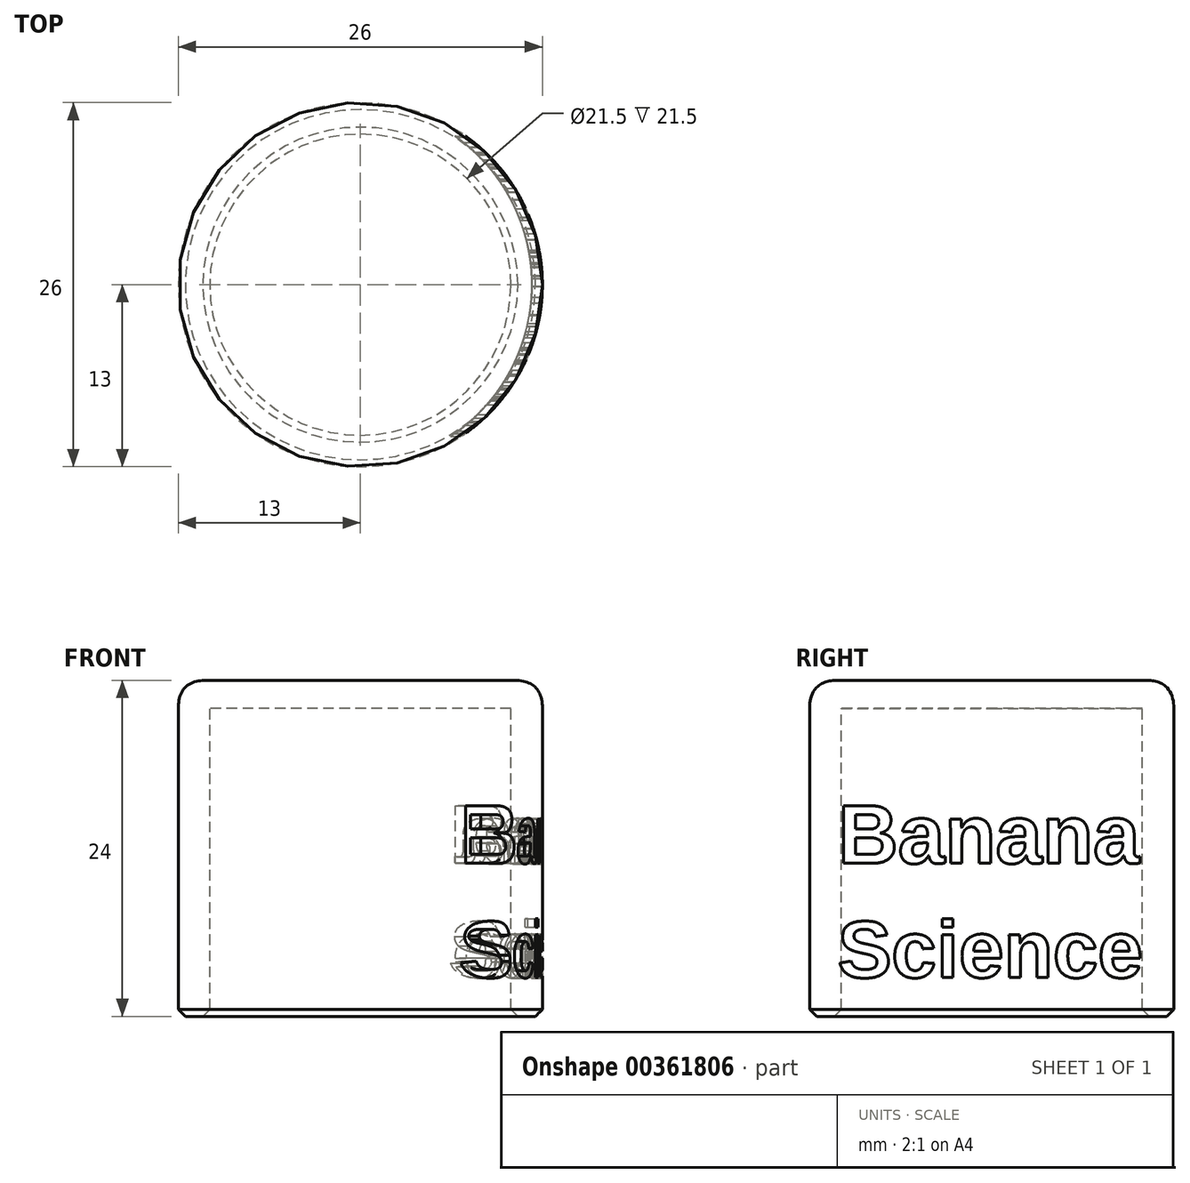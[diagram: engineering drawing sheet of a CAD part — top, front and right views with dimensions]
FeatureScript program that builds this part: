
annotation { "Feature Type Name" : "Feature", "Feature Type Description" : "" }
export const myFeature = defineFeature(function(context is Context, id is Id, definition is map)
    precondition{}
    {
        {
            var Q0;
            Q0=qCreatedBy(makeId("Top.planeOp"),FACE);
            var sketch = newSketch(context, id + "F0", { "sketchPlane" : qUnion([Q0])});
            skCircle(sketch, "E0", {"center": v(0, 0) * mm, "radius": 10.75 * mm});
            skCircle(sketch, "E1", {"center": v(0, 0) * mm, "radius": 13 * mm});
            skSolve(sketch);
        }
        {
            var Q0;
            Q0=makeQuery(id+"F0.imprint","IMPRINT",FACE,{"disambiguationData":[TD([[makeQuery(id+"F0.imprint","IMPRINT",EDGE,{"derivedFrom":sQuery(id+"F0.wireOp",EDGE,"E0")}),-1.0]])]});
            extrude(context, id + "F1", {"entities" : qUnion([Q0]), "oppositeDirection" : true, "depth" : 24 * mm, "offsetDistance" : 25 * mm});
        }
        {
            var Q0;
            Q0=makeQuery(id+"F0.imprint","IMPRINT",FACE,{"disambiguationData":[TD([[makeQuery(id+"F0.imprint","IMPRINT",EDGE,{"derivedFrom":sQuery(id+"F0.wireOp",EDGE,"E0")}),1.0]])]});
            extrude(context, id + "F2", {"entities" : qUnion([Q0]), "operationType" : NewBodyOperationType.ADD, "oppositeDirection" : true, "depth" : 2 * mm, "offsetDistance" : 25 * mm});
        }
        {
            var Q0;
            Q0=makeQuery(id+"F1.opExtrude","CAP_EDGE",EDGE,{"disambiguationData":[OSD([sQuery(id+"F0.wireOp",EDGE,"E1")])],"isStart":true});
            var Q1;
            Q1=makeQuery(id+"F2.opExtrude","CAP_EDGE",EDGE,{"disambiguationData":[OSD([sQuery(id+"F0.wireOp",EDGE,"E0")])],"isStart":false});
            fillet(context, id + "F3", {"entities" : qUnion([Q0, Q1]), "radius" : 2 * mm, "tangentPropagation" : true, "rho" : 0.5, "crossSection" : FilletCrossSection.CONIC, "allowEdgeOverflow" : false});
        }
        {
            var Q0;
            Q0=makeQuery(id+"F1.opExtrude","CAP_EDGE",EDGE,{"disambiguationData":[OSD([sQuery(id+"F0.wireOp",EDGE,"E0")])],"isStart":false});
            var Q1;
            Q1=makeQuery(id+"F1.opExtrude","CAP_EDGE",EDGE,{"disambiguationData":[OSD([sQuery(id+"F0.wireOp",EDGE,"E1")])],"isStart":false});
            var Q2;
            Q2=makeQuery(id+"F2.opExtrude","CAP_EDGE",EDGE,{"disambiguationData":[OSD([sQuery(id+"F0.wireOp",EDGE,"6ru0MfPZ-ubaX-B0dC-GUrv-7Vsd5N7kwgG7")])],"isStart":true});
            var Q3;
            Q3=makeQuery(id+"F2.opExtrude","CAP_EDGE",EDGE,{"disambiguationData":[OSD([sQuery(id+"F0.wireOp",EDGE,"6ru0MfPZ-ubaX-B0dC-GUrv-7Vsd5N7kwgG7")])],"isStart":false});
            chamfer(context, id + "F4", {"entities" : qUnion([Q0, Q1, Q2, Q3]), "width" : .5 * mm, "tangentPropagation" : true});
        }
        {
            var Q0;
            Q0=qCreatedBy(makeId("Right.planeOp"),FACE);
            cPlane(context, id + "F5", {"entities" : qUnion([Q0]), "cplaneType" : CPlaneType.OFFSET, "offset" : (26 / 2) * mm, "width" : 150 * mm, "height" : 150 * mm});
        }
        {
            var Q0;
            Q0=qCreatedBy(id+"F5.planeOp",FACE);
            var sketch = newSketch(context, id + "F6", { "sketchPlane" : qUnion([Q0])});
            skText(sketch, "E2", { "text": "Banana\n", "fontName": "Arimo-Bold.ttf"});
            skText(sketch, "E3", { "text": "Science", "fontName": "Arimo-Bold.ttf"});
            skLineSegment(sketch, "E4", {"start": v(0, -6.78) * mm, "end": v(0, -2) * mm, "construction": true});
            skLineSegment(sketch, "E5", {"start": v(0, -19.22) * mm, "end": v(0, -24) * mm, "construction": true});
            const initialGuessF6  = {"E2": [-0.011, -0.01307, 1, 0, 0.0043], "E3": [-0.011, -0.02122, 1, 0, 0.00415]};
            skSetInitialGuess(sketch, initialGuessF6);
            skSolve(sketch);
        }
        {
            var Q0;
            Q0=makeQuery(id+"F6.imprint","IMPRINT",FACE,{"disambiguationData":[TD([[makeQuery(id+"F6.imprint","IMPRINT",EDGE,{"derivedFrom":sQuery(id+"F6.wireOp",EDGE,"E2.sketch_text.stroke-0")}),-1.0]])]});
            var Q1;
            Q1=makeQuery(id+"F6.imprint","IMPRINT",FACE,{"disambiguationData":[TD([[makeQuery(id+"F6.imprint","IMPRINT",EDGE,{"derivedFrom":sQuery(id+"F6.wireOp",EDGE,"E2.sketch_text.stroke-24")}),-1.0]])]});
            var Q2;
            Q2=makeQuery(id+"F6.imprint","IMPRINT",FACE,{"disambiguationData":[TD([[makeQuery(id+"F6.imprint","IMPRINT",EDGE,{"derivedFrom":sQuery(id+"F6.wireOp",EDGE,"E2.sketch_text.stroke-62")}),-1.0]])]});
            var Q3;
            Q3=makeQuery(id+"F6.imprint","IMPRINT",FACE,{"disambiguationData":[TD([[makeQuery(id+"F6.imprint","IMPRINT",EDGE,{"derivedFrom":sQuery(id+"F6.wireOp",EDGE,"E2.sketch_text.stroke-81")}),-1.0]])]});
            var Q4;
            Q4=makeQuery(id+"F6.imprint","IMPRINT",FACE,{"disambiguationData":[TD([[makeQuery(id+"F6.imprint","IMPRINT",EDGE,{"derivedFrom":sQuery(id+"F6.wireOp",EDGE,"E3.sketch_text.stroke-0")}),-1.0]])]});
            var Q5;
            Q5=makeQuery(id+"F6.imprint","IMPRINT",FACE,{"disambiguationData":[TD([[makeQuery(id+"F6.imprint","IMPRINT",EDGE,{"derivedFrom":sQuery(id+"F6.wireOp",EDGE,"E3.sketch_text.stroke-31")}),-1.0]])]});
            var Q6;
            Q6=makeQuery(id+"F6.imprint","IMPRINT",FACE,{"disambiguationData":[TD([[makeQuery(id+"F6.imprint","IMPRINT",EDGE,{"derivedFrom":sQuery(id+"F6.wireOp",EDGE,"E3.sketch_text.stroke-52")}),-1.0]])]});
            var Q7;
            Q7=makeQuery(id+"F6.imprint","IMPRINT",FACE,{"disambiguationData":[TD([[makeQuery(id+"F6.imprint","IMPRINT",EDGE,{"derivedFrom":sQuery(id+"F6.wireOp",EDGE,"E3.sketch_text.stroke-48")}),-1.0]])]});
            var Q8;
            Q8=makeQuery(id+"F6.imprint","IMPRINT",FACE,{"disambiguationData":[TD([[makeQuery(id+"F6.imprint","IMPRINT",EDGE,{"derivedFrom":sQuery(id+"F6.wireOp",EDGE,"E3.sketch_text.stroke-56")}),-1.0]])]});
            var Q9;
            Q9=makeQuery(id+"F6.imprint","IMPRINT",FACE,{"disambiguationData":[TD([[makeQuery(id+"F6.imprint","IMPRINT",EDGE,{"derivedFrom":sQuery(id+"F6.wireOp",EDGE,"E3.sketch_text.stroke-74")}),-1.0]])]});
            var Q10;
            Q10=makeQuery(id+"F6.imprint","IMPRINT",FACE,{"disambiguationData":[TD([[makeQuery(id+"F6.imprint","IMPRINT",EDGE,{"derivedFrom":sQuery(id+"F6.wireOp",EDGE,"E3.sketch_text.stroke-93")}),-1.0]])]});
            var Q11;
            Q11=makeQuery(id+"F6.imprint","IMPRINT",FACE,{"disambiguationData":[TD([[makeQuery(id+"F6.imprint","IMPRINT",EDGE,{"derivedFrom":sQuery(id+"F6.wireOp",EDGE,"E3.sketch_text.stroke-110")}),-1.0]])]});
            var Q12;
            Q12=makeQuery(id+"F6.imprint","IMPRINT",FACE,{"disambiguationData":[TD([[makeQuery(id+"F6.imprint","IMPRINT",EDGE,{"derivedFrom":sQuery(id+"F6.wireOp",EDGE,"E2.sketch_text.stroke-119")}),-1.0]])]});
            var Q13;
            Q13=makeQuery(id+"F6.imprint","IMPRINT",FACE,{"disambiguationData":[TD([[makeQuery(id+"F6.imprint","IMPRINT",EDGE,{"derivedFrom":sQuery(id+"F6.wireOp",EDGE,"E2.sketch_text.stroke-138")}),-1.0]])]});
            var Q14;
            Q14=makeQuery(id+"F1.opExtrude","SWEPT_FACE",FACE,{"disambiguationData":[OSD([sQuery(id+"F0.wireOp",EDGE,"E1")])]});
            extrude(context, id + "F7", {"entities" : qUnion([Q0, Q1, Q2, Q3, Q4, Q5, Q6, Q7, Q8, Q9, Q10, Q11, Q12, Q13]), "operationType" : NewBodyOperationType.REMOVE, "endBound" : BoundingType.UP_TO_SURFACE, "oppositeDirection" : true, "depth" : 25 * mm, "endBoundEntityFace" : qUnion([Q14]), "hasOffset" : true, "offsetDistance" : .75 * mm, "offsetOppositeDirection" : true});
        }
    });
